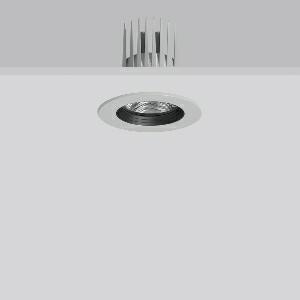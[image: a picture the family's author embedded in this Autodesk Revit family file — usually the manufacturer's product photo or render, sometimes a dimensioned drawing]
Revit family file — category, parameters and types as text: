
# Revit family: heledon_mini_e_901750_004_2_819e
name_source: partatom
category: Lighting Fixtures
units: mm (PartAtom-declared; Revit-internal decimal feet)

## family parameters
Cut with Voids When Loaded = No
Host = Face
Light Source = No
Part Type = Normal
Room Calculation Point = No
Round Connector Dimension = Use Diameter
Shared = No

## types (1)
- HELEDON mini E (1 x LED Modul 927, 3500 lm, 2700)
    Apparent Load = 29 VA
    Approval mark = CE
    CIE Flux Codes = 95 99 100 100 100
    Color Rendering = 92
    Color Temperature = 2700
    Default Elevation = 1800 mm
    Description = Series: HELEDON mini
Round recessed downlight. Housing: die-cast aluminium, powder-coated. Black plastic ring and recessed LED to prevent glare from the side. Optical assembly with reflector made of MIRO-Silver with 98% total light reflection for outstanding efficiency - can be changed without tools. Best colour rendering index Ra>90. Suitable for Recessed ceiling mounting. Installation without tools thanks to spring fastening system. Including separate LED converter with connecting cable 600 mm.High quality converter without flickering and stroboscopic effect. Through-wiring box (5 pole) available as accessory. The following accessories can be mounted without use of tools: interchangeable lenses, decorative glasses, honeycomb louvre, clear and frosted diffusers, white interchangeable plastic ring. 
Colour: silver
Diameter: 124 mm
Height: 3 mm
Cut-out diameter: 114 mm
Recess height: 170 mm
Luminaire: recess height: 120 mm
Lamp: LED
Socket: without socket
Colour temperature: 2700K
Colour rendering index (CRI): 92
System power: 29 W
Rated luminous flux: 3500 lm
Luminous efficiency: 121 lm/W
Control gear: Regulated power supply
Protection class: II
Type of protection: IP 20
    Height = 0 mm  [stored 0 ft]
    Lamp = 1 x LED Modul 927
    Lamp Light Flux = 3500 lm
    Lamp count = 1
    Length = 124 mm  [stored 0.406824 ft]
    Lifetime = 50000 h
    Luminous efficacy = 121 lm/W
    Manufacturer = RZB
    ModVariant = No
    Model = 901750.004.2
    Mounting Place = Ceiling
    Mounting Type = Recessed
    Number of Poles = 1
    OnlyDefault = Yes
    Power Factor = 1
    Product Name = HELEDON mini E
    Product group = Recessed downlights
    ProductGroupID = 402
    Protection Class = Protection class II
    Protection Degree = IP 20
    RLX_Detail_Level = 1
    RLX_Emergency_Light_Flux = 0 lm
    RLX_Emergency_Type = 0
    RLX_Emergency_Type_DB = No
    RlxData = <blob elided: 126741 chars, md5=d68318a4>
    Socket = socket
    Standby Power = 0 W
    System Light Flux = 3500 lm
    System Power = 29 W
    Type Comments = Product without accessories
    Type Image = 901657.004.jpg
    URL = http://relux.com
    VarID = ---
    Voltage = 230 V
    Voltage Range = 220-240 V
    Weight = 0.00 kg
    Width = 0 mm  [stored 0 ft]

note: [stored X ft] marks values corroborated as IEEE doubles in the binary element streams (Revit-internal decimal feet)

## geometry (parser evidence)
native form markers: Blend x4, Sweep x11
no freeform markers — native parametric forms only
